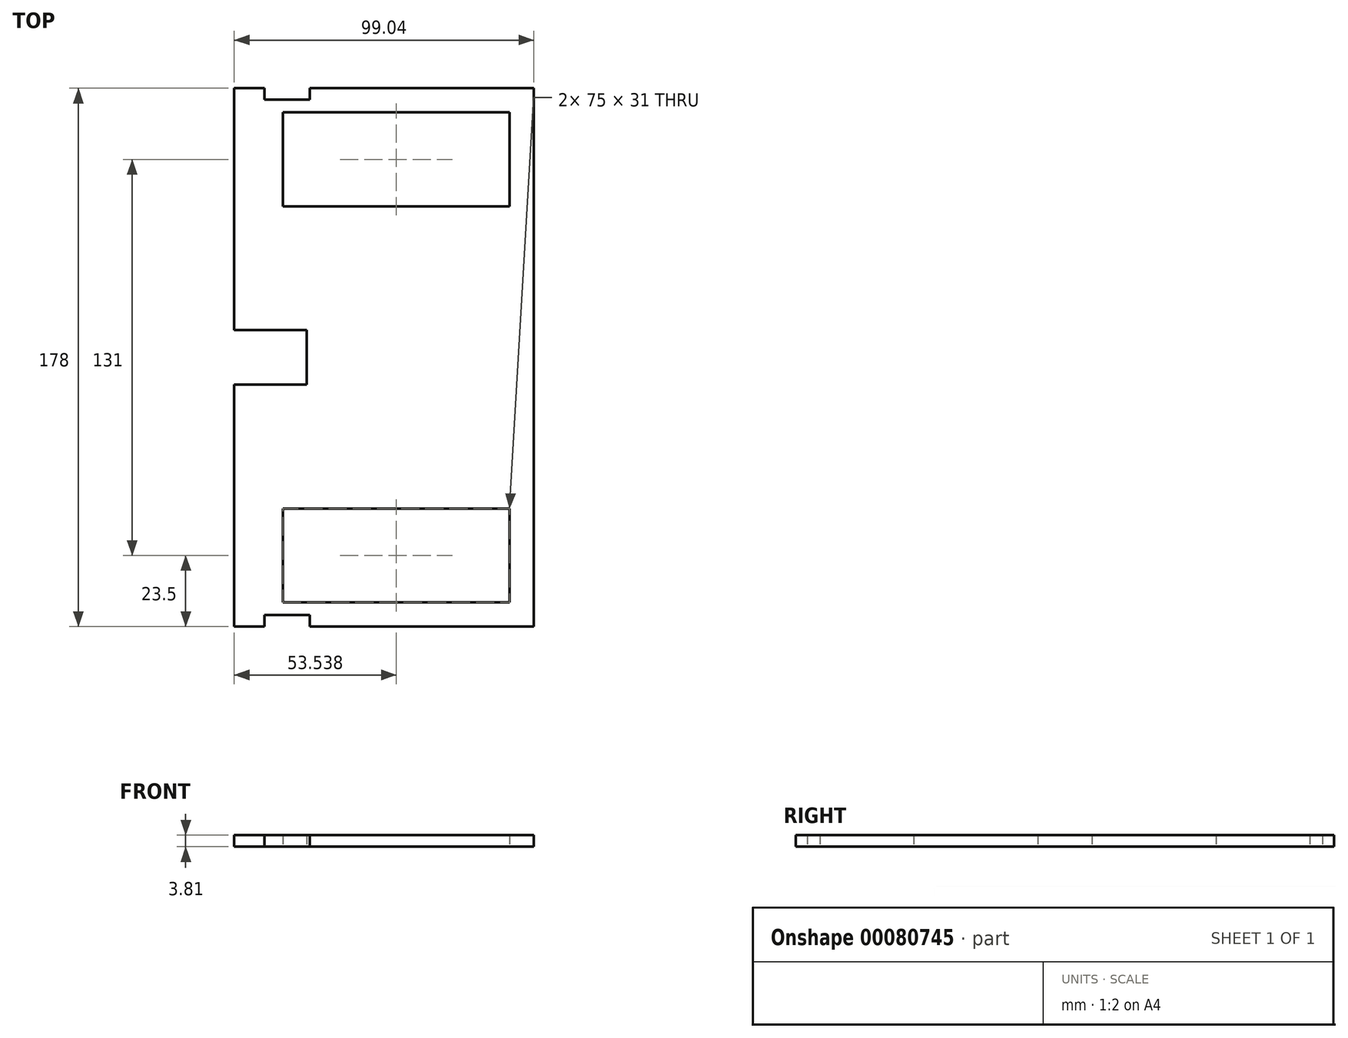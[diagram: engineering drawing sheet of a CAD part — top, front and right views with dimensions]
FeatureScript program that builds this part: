
annotation { "Feature Type Name" : "Feature", "Feature Type Description" : "" }
export const myFeature = defineFeature(function(context is Context, id is Id, definition is map)
    precondition{}
    {
        {
            var Q0;
            Q0=qCreatedBy(makeId("Top.planeOp"),FACE);
            var sketch = newSketch(context, id + "F0", { "sketchPlane" : qUnion([Q0])});
            skLineSegment(sketch, "E0.bottom", {"start": v(49.52, 89) * mm, "end": v(-49.52, 89) * mm});
            skLineSegment(sketch, "E0.top", {"start": v(49.52, -89) * mm, "end": v(-49.52, -89) * mm});
            skLineSegment(sketch, "E0.left", {"start": v(49.52, 89) * mm, "end": v(49.52, -89) * mm});
            skLineSegment(sketch, "E0.right", {"start": v(-49.52, 89) * mm, "end": v(-49.52, -89) * mm});
            skPoint(sketch, "E0.middle", {"position": v(0, 0) * mm});
            skLineSegment(sketch, "E1.bottom", {"start": v(41.52, 81) * mm, "end": v(-33.48, 81) * mm});
            skLineSegment(sketch, "E1.top", {"start": v(41.52, 50) * mm, "end": v(-33.48, 50) * mm});
            skLineSegment(sketch, "E1.left", {"start": v(41.52, 81) * mm, "end": v(41.52, 50) * mm});
            skLineSegment(sketch, "E1.right", {"start": v(-33.48, 81) * mm, "end": v(-33.48, 50) * mm});
            skPoint(sketch, "E1.middle", {"position": v(4.02, 65.5) * mm});
            skLineSegment(sketch, "E2", {"start": v(-49.52, 0) * mm, "end": v(49.52, 0) * mm, "construction": true});
            skLineSegment(sketch, "E3.MirrorCS", {"start": v(-33.48, -81) * mm, "end": v(-33.48, -50) * mm});
            skLineSegment(sketch, "E4.MirrorCS", {"start": v(41.52, -81) * mm, "end": v(-33.48, -81) * mm});
            skLineSegment(sketch, "E5.MirrorCS", {"start": v(41.52, -81) * mm, "end": v(41.52, -50) * mm});
            skLineSegment(sketch, "E6.MirrorCS", {"start": v(41.52, -50) * mm, "end": v(-33.48, -50) * mm});
            skLineSegment(sketch, "E7", {"start": v(-49.52, 9) * mm, "end": v(-25.52, 9) * mm});
            skLineSegment(sketch, "E8", {"start": v(-25.52, 9) * mm, "end": v(-25.52, 0) * mm});
            skLineSegment(sketch, "E9.MirrorCS", {"start": v(-25.52, -9) * mm, "end": v(-25.52, 0) * mm});
            skLineSegment(sketch, "E10.MirrorCS", {"start": v(-49.52, -9) * mm, "end": v(-25.52, -9) * mm});
            skLineSegment(sketch, "E11", {"start": v(-39.52, -89) * mm, "end": v(-39.52, -85.19) * mm});
            skLineSegment(sketch, "E12", {"start": v(-39.52, -85.19) * mm, "end": v(-24.52, -85.19) * mm});
            skLineSegment(sketch, "E13", {"start": v(-24.52, -85.19) * mm, "end": v(-24.52, -89) * mm});
            skLineSegment(sketch, "E14.MirrorCS", {"start": v(-39.52, 85.19) * mm, "end": v(-24.52, 85.19) * mm});
            skLineSegment(sketch, "E15.MirrorCS", {"start": v(-39.52, 89) * mm, "end": v(-39.52, 85.19) * mm});
            skLineSegment(sketch, "E16.MirrorCS", {"start": v(-24.52, 85.19) * mm, "end": v(-24.52, 89) * mm});
            skLineSegment(sketch, "E17", {"start": v(49.52, 79) * mm, "end": v(45.7, 79) * mm});
            skLineSegment(sketch, "E18", {"start": v(45.7, 79) * mm, "end": v(45.7, 64) * mm});
            skLineSegment(sketch, "E19", {"start": v(45.7, 64) * mm, "end": v(49.52, 64) * mm});
            skLineSegment(sketch, "E20", {"start": v(49.52, 54) * mm, "end": v(45.7, 54) * mm});
            skLineSegment(sketch, "E21", {"start": v(45.7, 54) * mm, "end": v(45.7, 39) * mm});
            skLineSegment(sketch, "E22", {"start": v(45.7, 39) * mm, "end": v(49.52, 39) * mm});
            skLineSegment(sketch, "E23.MirrorCS", {"start": v(45.7, -39) * mm, "end": v(49.52, -39) * mm});
            skLineSegment(sketch, "E24.MirrorCS", {"start": v(45.7, -54) * mm, "end": v(45.7, -39) * mm});
            skLineSegment(sketch, "E25.MirrorCS", {"start": v(49.52, -54) * mm, "end": v(45.7, -54) * mm});
            skLineSegment(sketch, "E26.MirrorCS", {"start": v(45.7, -64) * mm, "end": v(49.52, -64) * mm});
            skLineSegment(sketch, "E27.MirrorCS", {"start": v(45.7, -79) * mm, "end": v(45.7, -64) * mm});
            skLineSegment(sketch, "E28.MirrorCS", {"start": v(49.52, -79) * mm, "end": v(45.7, -79) * mm});
            skLineSegment(sketch, "E29", {"start": v(-49.52, 68.5) * mm, "end": v(-45.7, 68.5) * mm});
            skLineSegment(sketch, "E30", {"start": v(-45.7, 68.5) * mm, "end": v(-45.7, 53.5) * mm});
            skLineSegment(sketch, "E31", {"start": v(-45.7, 53.5) * mm, "end": v(-49.52, 53.5) * mm});
            skLineSegment(sketch, "E32", {"start": v(-49.52, 36) * mm, "end": v(-45.7, 36) * mm});
            skLineSegment(sketch, "E33", {"start": v(-45.7, 36) * mm, "end": v(-45.7, 21) * mm});
            skLineSegment(sketch, "E34", {"start": v(-45.7, 21) * mm, "end": v(-49.52, 21) * mm});
            skLineSegment(sketch, "E35.MirrorCS", {"start": v(-45.7, -36) * mm, "end": v(-45.7, -21) * mm});
            skLineSegment(sketch, "E36.MirrorCS", {"start": v(-45.7, -21) * mm, "end": v(-49.52, -21) * mm});
            skLineSegment(sketch, "E37.MirrorCS", {"start": v(-49.52, -36) * mm, "end": v(-45.7, -36) * mm});
            skLineSegment(sketch, "E38.MirrorCS", {"start": v(-45.7, -53.5) * mm, "end": v(-49.52, -53.5) * mm});
            skLineSegment(sketch, "E39.MirrorCS", {"start": v(-45.7, -68.5) * mm, "end": v(-45.7, -53.5) * mm});
            skLineSegment(sketch, "E40.MirrorCS", {"start": v(-49.52, -68.5) * mm, "end": v(-45.7, -68.5) * mm});
            skSolve(sketch);
        }
        {
            var Q0;
            Q0=makeQuery(id+"F0.imprint","IMPRINT",FACE,{"disambiguationData":[TD([[makeQuery(id+"F0.imprint","IMPRINT",EDGE,{"derivedFrom":sQuery(id+"F0.wireOp",EDGE,"E0.bottom")}),1.0]])]});
            var Q1;
            {var subQ0=sQuery(id+"F0.wireOp",EDGE,"E26.MirrorCS");Q1=makeQuery(id+"F0.imprint","IMPRINT",FACE,{"disambiguationData":[TD([[makeQuery(id+"F0.imprint","IMPRINT",EDGE,{"derivedFrom":subQ0}),-1.0]])]});}
            var Q2;
            {var subQ0=sQuery(id+"F0.wireOp",EDGE,"E23.MirrorCS");Q2=makeQuery(id+"F0.imprint","IMPRINT",FACE,{"disambiguationData":[TD([[makeQuery(id+"F0.imprint","IMPRINT",EDGE,{"derivedFrom":subQ0}),-1.0]])]});}
            var Q3;
            {var subQ0=sQuery(id+"F0.wireOp",EDGE,"E20");Q3=makeQuery(id+"F0.imprint","IMPRINT",FACE,{"disambiguationData":[TD([[makeQuery(id+"F0.imprint","IMPRINT",EDGE,{"derivedFrom":subQ0}),1.0]])]});}
            var Q4;
            {var subQ0=sQuery(id+"F0.wireOp",EDGE,"E17");Q4=makeQuery(id+"F0.imprint","IMPRINT",FACE,{"disambiguationData":[TD([[makeQuery(id+"F0.imprint","IMPRINT",EDGE,{"derivedFrom":subQ0}),1.0]])]});}
            var Q5;
            {var subQ0=sQuery(id+"F0.wireOp",EDGE,"E29");Q5=makeQuery(id+"F0.imprint","IMPRINT",FACE,{"disambiguationData":[TD([[makeQuery(id+"F0.imprint","IMPRINT",EDGE,{"derivedFrom":subQ0}),-1.0]])]});}
            var Q6;
            Q6=makeQuery(id+"F0.imprint","IMPRINT",FACE,{"disambiguationData":[TD([[makeQuery(id+"F0.imprint","IMPRINT",EDGE,{"derivedFrom":sQuery(id+"F0.wireOp",EDGE,"E35.MirrorCS")}),1.0]])]});
            var Q7;
            {var subQ0=sQuery(id+"F0.wireOp",EDGE,"E38.MirrorCS");Q7=makeQuery(id+"F0.imprint","IMPRINT",FACE,{"disambiguationData":[TD([[makeQuery(id+"F0.imprint","IMPRINT",EDGE,{"derivedFrom":subQ0}),1.0]])]});}
            var Q8;
            {var subQ0=sQuery(id+"F0.wireOp",EDGE,"E32");Q8=makeQuery(id+"F0.imprint","IMPRINT",FACE,{"disambiguationData":[TD([[makeQuery(id+"F0.imprint","IMPRINT",EDGE,{"derivedFrom":subQ0}),-1.0]])]});}
            extrude(context, id + "F1", {"entities" : qUnion([Q0, Q1, Q2, Q3, Q4, Q5, Q6, Q7, Q8]), "depth" : 3.8 * mm});
        }
    });
